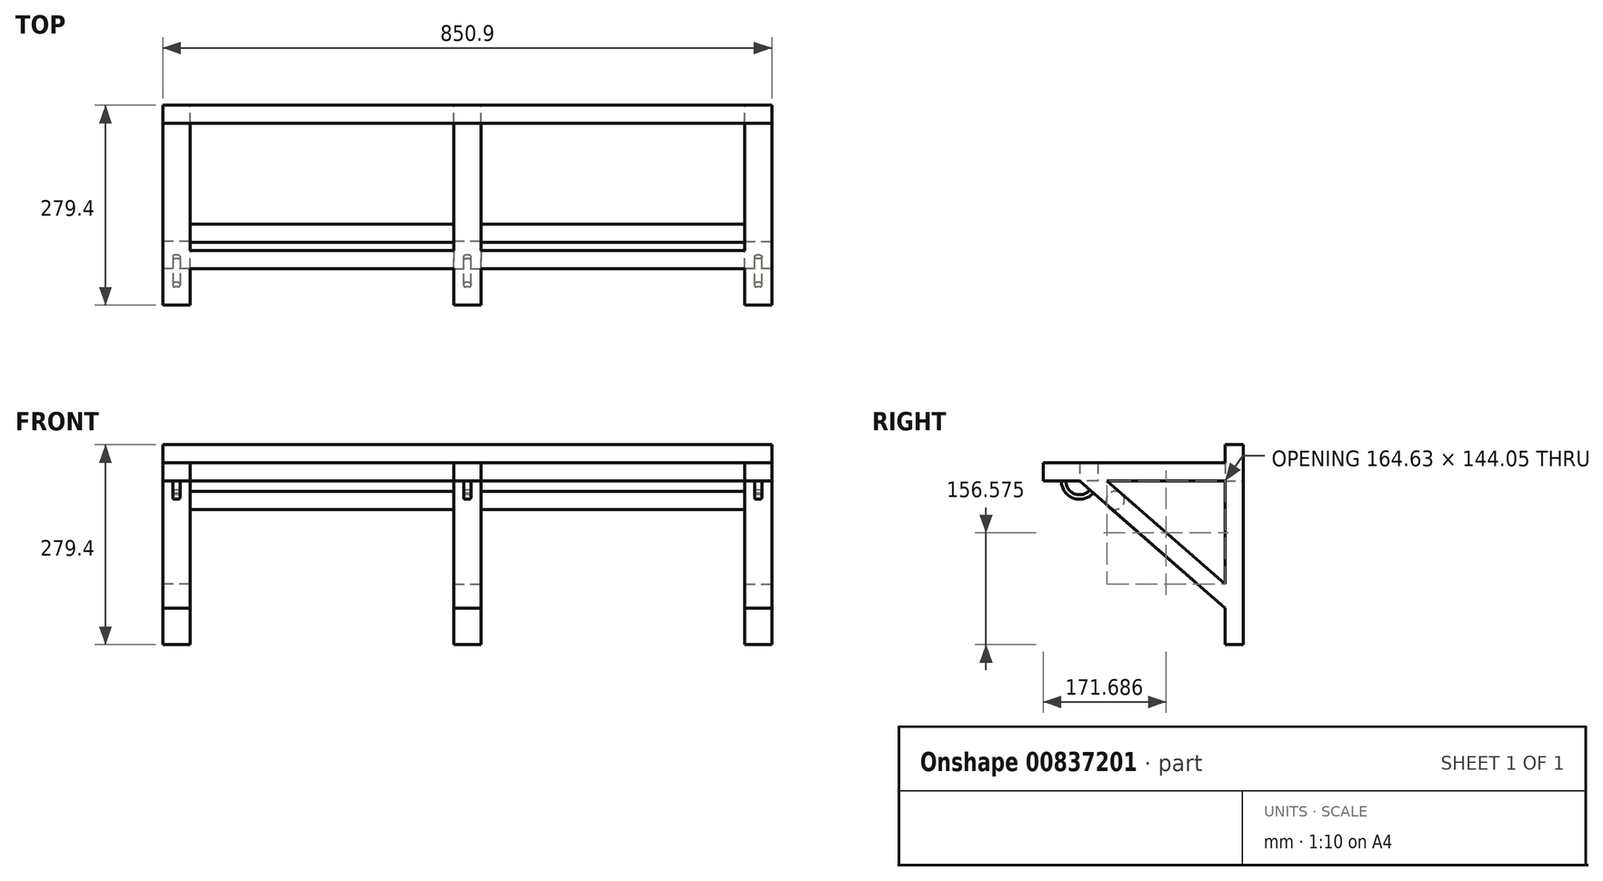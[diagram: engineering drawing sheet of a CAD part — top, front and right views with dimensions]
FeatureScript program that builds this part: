
annotation { "Feature Type Name" : "Feature", "Feature Type Description" : "" }
export const myFeature = defineFeature(function(context is Context, id is Id, definition is map)
    precondition{}
    {
        {
            var Q0;
            Q0=qCreatedBy(makeId("Front.planeOp"),FACE);
            var sketch = newSketch(context, id + "F0", { "sketchPlane" : qUnion([Q0])});
            skLineSegment(sketch, "E0.bottom", {"start": v(19.05, -139.7) * mm, "end": v(-19.05, -139.7) * mm});
            skLineSegment(sketch, "E0.top", {"start": v(19.05, 139.7) * mm, "end": v(-19.05, 139.7) * mm});
            skLineSegment(sketch, "E0.left", {"start": v(19.05, -139.7) * mm, "end": v(19.05, 139.7) * mm});
            skLineSegment(sketch, "E0.right", {"start": v(-19.05, -139.7) * mm, "end": v(-19.05, 139.7) * mm});
            skPoint(sketch, "E0.middle", {"position": v(0, 0) * mm});
            skLineSegment(sketch, "E1.bottom", {"start": v(-387.35, -139.7) * mm, "end": v(-425.45, -139.7) * mm});
            skLineSegment(sketch, "E1.top", {"start": v(-387.35, 139.7) * mm, "end": v(-425.45, 139.7) * mm});
            skLineSegment(sketch, "E1.left", {"start": v(-387.35, -139.7) * mm, "end": v(-387.35, 139.7) * mm});
            skLineSegment(sketch, "E1.right", {"start": v(-425.45, -139.7) * mm, "end": v(-425.45, 139.7) * mm});
            skPoint(sketch, "E1.middle", {"position": v(-406.4, 0) * mm});
            skLineSegment(sketch, "E2.bottom", {"start": v(425.45, -139.7) * mm, "end": v(387.35, -139.7) * mm});
            skLineSegment(sketch, "E2.top", {"start": v(425.45, 139.7) * mm, "end": v(387.35, 139.7) * mm});
            skLineSegment(sketch, "E2.left", {"start": v(425.45, -139.7) * mm, "end": v(425.45, 139.7) * mm});
            skLineSegment(sketch, "E2.right", {"start": v(387.35, -139.7) * mm, "end": v(387.35, 139.7) * mm});
            skPoint(sketch, "E2.middle", {"position": v(406.4, 0) * mm});
            skLineSegment(sketch, "E3.bottom", {"start": v(425.45, 88.9) * mm, "end": v(-425.45, 88.9) * mm});
            skLineSegment(sketch, "E3.top", {"start": v(425.45, 114.3) * mm, "end": v(-425.45, 114.3) * mm});
            skLineSegment(sketch, "E3.left", {"start": v(425.45, 88.9) * mm, "end": v(425.45, 114.3) * mm});
            skLineSegment(sketch, "E3.right", {"start": v(-425.45, 88.9) * mm, "end": v(-425.45, 114.3) * mm});
            skPoint(sketch, "E3.middle", {"position": v(0, 101.6) * mm});
            skSolve(sketch);
        }
        {
            var Q0;
            Q0 = qSketchRegion(id + "F0", true);
            extrude(context, id + "F1", {"entities" : qUnion([Q0]), "depth" : 25.4 * mm, "offsetDistance" : 25.4 * mm});
        }
        {
            var Q0;
            Q0=makeQuery(id+"F1.opExtrude","CAP_FACE",FACE,{"disambiguationData":[OSD([sQuery(id+"F0.wireOp",EDGE,"E0.bottom"),sQuery(id+"F0.wireOp",EDGE,"E0.top"),sQuery(id+"F0.wireOp",EDGE,"E0.left"),sQuery(id+"F0.wireOp",EDGE,"E0.right"),sQuery(id+"F0.wireOp",EDGE,"E1.bottom"),sQuery(id+"F0.wireOp",EDGE,"E1.top"),sQuery(id+"F0.wireOp",EDGE,"E1.left"),sQuery(id+"F0.wireOp",EDGE,"E1.right"),sQuery(id+"F0.wireOp",EDGE,"E2.bottom"),sQuery(id+"F0.wireOp",EDGE,"E2.top"),sQuery(id+"F0.wireOp",EDGE,"E2.left"),sQuery(id+"F0.wireOp",EDGE,"E2.right"),sQuery(id+"F0.wireOp",EDGE,"E3.bottom"),sQuery(id+"F0.wireOp",EDGE,"E3.top"),sQuery(id+"F0.wireOp",EDGE,"E3.left"),sQuery(id+"F0.wireOp",EDGE,"E3.right")])],"isStart":false});
            var sketch = newSketch(context, id + "F2", { "sketchPlane" : qUnion([Q0])});
            skLineSegment(sketch, "E4.bottom", {"start": v(-387.35, 88.9) * mm, "end": v(-425.45, 88.9) * mm});
            skLineSegment(sketch, "E4.top", {"start": v(-387.35, 114.3) * mm, "end": v(-425.45, 114.3) * mm});
            skLineSegment(sketch, "E4.left", {"start": v(-387.35, 88.9) * mm, "end": v(-387.35, 114.3) * mm});
            skLineSegment(sketch, "E4.right", {"start": v(-425.45, 88.9) * mm, "end": v(-425.45, 114.3) * mm});
            skLineSegment(sketch, "E5.bottom", {"start": v(-19.05, 114.3) * mm, "end": v(19.05, 114.3) * mm});
            skLineSegment(sketch, "E5.top", {"start": v(-19.05, 88.9) * mm, "end": v(19.05, 88.9) * mm});
            skLineSegment(sketch, "E5.left", {"start": v(-19.05, 114.3) * mm, "end": v(-19.05, 88.9) * mm});
            skLineSegment(sketch, "E5.right", {"start": v(19.05, 114.3) * mm, "end": v(19.05, 88.9) * mm});
            skLineSegment(sketch, "E6.bottom", {"start": v(387.35, 114.3) * mm, "end": v(425.45, 114.3) * mm});
            skLineSegment(sketch, "E6.top", {"start": v(387.35, 88.9) * mm, "end": v(425.45, 88.9) * mm});
            skLineSegment(sketch, "E6.left", {"start": v(387.35, 114.3) * mm, "end": v(387.35, 88.9) * mm});
            skLineSegment(sketch, "E6.right", {"start": v(425.45, 114.3) * mm, "end": v(425.45, 88.9) * mm});
            skSolve(sketch);
        }
        {
            var Q0;
            Q0 = qSketchRegion(id + "F2", true);
            extrude(context, id + "F3", {"entities" : qUnion([Q0]), "operationType" : NewBodyOperationType.ADD, "depth" : 203.2 * mm, "offsetDistance" : 25.4 * mm});
        }
        {
            var Q0;
            Q0=makeQuery(id+"F3.opExtrude","SWEPT_FACE",FACE,{"disambiguationData":[OSD([sQuery(id+"F2.wireOp",EDGE,"E4.top")])]});
            var sketch = newSketch(context, id + "F4", { "sketchPlane" : qUnion([Q0])});
            skLineSegment(sketch, "E7.bottom", {"start": v(-425.45, -228.6) * mm, "end": v(425.45, -228.6) * mm});
            skLineSegment(sketch, "E7.top", {"start": v(-425.45, -203.2) * mm, "end": v(425.45, -203.2) * mm});
            skLineSegment(sketch, "E7.left", {"start": v(-425.45, -228.6) * mm, "end": v(-425.45, -203.2) * mm});
            skLineSegment(sketch, "E7.right", {"start": v(425.45, -228.6) * mm, "end": v(425.45, -203.2) * mm});
            skSolve(sketch);
        }
        {
            var Q0;
            Q0 = qSketchRegion(id + "F4", true);
            extrude(context, id + "F5", {"entities" : qUnion([Q0]), "operationType" : NewBodyOperationType.ADD, "oppositeDirection" : true, "depth" : 25.4 * mm, "offsetDistance" : 25.4 * mm});
        }
        {
            var Q0;
            Q0=makeQuery(id+"F3.boolean.opBoolean","MERGE",FACE,{"derivedFrom":[makeQuery(id+"F1.opExtrude","SWEPT_FACE",FACE,{"disambiguationData":[OSD([sQuery(id+"F0.wireOp",EDGE,"E1.right"),sQuery(id+"F0.wireOp",EDGE,"E3.right")])]}),makeQuery(id+"F3.opExtrude","SWEPT_FACE",FACE,{"disambiguationData":[OSD([sQuery(id+"F2.wireOp",EDGE,"E4.right")])]})]});
            var sketch = newSketch(context, id + "F6", { "sketchPlane" : qUnion([Q0])});
            skLineSegment(sketch, "E8", {"start": v(228.6, 88.9) * mm, "end": v(25.4, -88.9) * mm});
            skLineSegment(sketch, "E9", {"start": v(25.4, -88.9) * mm, "end": v(25.4, -55.15) * mm});
            skLineSegment(sketch, "E10", {"start": v(25.4, -55.15) * mm, "end": v(190.03, 88.9) * mm});
            skLineSegment(sketch, "E11", {"start": v(190.03, 88.9) * mm, "end": v(228.6, 88.9) * mm});
            skSolve(sketch);
        }
        {
            var Q0;
            Q0 = qSketchRegion(id + "F6", true);
            extrude(context, id + "F7", {"entities" : qUnion([Q0]), "operationType" : NewBodyOperationType.ADD, "oppositeDirection" : true, "depth" : 38.1 * mm, "offsetDistance" : 25.4 * mm});
        }
        {
            var Q0;
            Q0=makeQuery(id+"F3.boolean.opBoolean","MERGE",FACE,{"derivedFrom":[makeQuery(id+"F1.opExtrude","SWEPT_FACE",FACE,{"disambiguationData":[OSD([sQuery(id+"F0.wireOp",EDGE,"E2.left"),sQuery(id+"F0.wireOp",EDGE,"E3.left")])]}),makeQuery(id+"F3.opExtrude","SWEPT_FACE",FACE,{"disambiguationData":[OSD([sQuery(id+"F2.wireOp",EDGE,"E6.right")])]})]});
            var sketch = newSketch(context, id + "F8", { "sketchPlane" : qUnion([Q0])});
            skLineSegment(sketch, "E12", {"start": v(-190.03, 88.9) * mm, "end": v(-25.4, -55.15) * mm});
            skLineSegment(sketch, "E13", {"start": v(-228.6, 88.9) * mm, "end": v(-25.4, -88.9) * mm});
            skLineSegment(sketch, "E14", {"start": v(-190.03, 88.9) * mm, "end": v(-228.6, 88.9) * mm});
            skLineSegment(sketch, "E15", {"start": v(-25.4, -88.9) * mm, "end": v(-25.4, -55.15) * mm});
            skSolve(sketch);
        }
        {
            var Q0;
            Q0 = qSketchRegion(id + "F8", true);
            extrude(context, id + "F9", {"entities" : qUnion([Q0]), "operationType" : NewBodyOperationType.ADD, "oppositeDirection" : true, "depth" : 38.1 * mm, "offsetDistance" : 25.4 * mm});
        }
        {
            var Q0;
            Q0 = qSketchRegion(id + "F6", true);
            extrude(context, id + "F10", {"entities" : qUnion([Q0]), "operationType" : NewBodyOperationType.ADD, "oppositeDirection" : true, "depth" : 38.1 * mm, "offsetDistance" : 25.4 * mm});
        }
        {
            var Q0;
            Q0=makeQuery(id+"F5.boolean.opBoolean","MERGE",FACE,{"derivedFrom":[makeQuery(id+"F3.opExtrude","SWEPT_FACE",FACE,{"disambiguationData":[OSD([sQuery(id+"F2.wireOp",EDGE,"E4.top")])]}),makeQuery(id+"F3.opExtrude","SWEPT_FACE",FACE,{"disambiguationData":[OSD([sQuery(id+"F2.wireOp",EDGE,"E5.bottom")])]}),makeQuery(id+"F3.opExtrude","SWEPT_FACE",FACE,{"disambiguationData":[OSD([sQuery(id+"F2.wireOp",EDGE,"E6.bottom")])]}),makeQuery(id+"F5.opExtrude","CAP_FACE",FACE,{"disambiguationData":[OSD([sQuery(id+"F4.wireOp",EDGE,"E7.bottom"),sQuery(id+"F4.wireOp",EDGE,"E7.top"),sQuery(id+"F4.wireOp",EDGE,"E7.left"),sQuery(id+"F4.wireOp",EDGE,"E7.right")])],"isStart":true})]});
            var sketch = newSketch(context, id + "F11", { "sketchPlane" : qUnion([Q0])});
            skLineSegment(sketch, "E16.top", {"start": v(-425.45, -279.4) * mm, "end": v(-387.35, -279.4) * mm});
            skLineSegment(sketch, "E16.left", {"start": v(-425.45, -228.6) * mm, "end": v(-425.45, -279.4) * mm});
            skLineSegment(sketch, "E16.right", {"start": v(-387.35, -228.6) * mm, "end": v(-387.35, -279.4) * mm});
            skLineSegment(sketch, "E17.top", {"start": v(-19.05, -279.4) * mm, "end": v(19.05, -279.4) * mm});
            skLineSegment(sketch, "E17.left", {"start": v(-19.05, -228.6) * mm, "end": v(-19.05, -279.4) * mm});
            skLineSegment(sketch, "E17.right", {"start": v(19.05, -228.6) * mm, "end": v(19.05, -279.4) * mm});
            skLineSegment(sketch, "E18.top", {"start": v(387.35, -279.4) * mm, "end": v(425.45, -279.4) * mm});
            skLineSegment(sketch, "E18.left", {"start": v(387.35, -228.6) * mm, "end": v(387.35, -279.4) * mm});
            skLineSegment(sketch, "E18.right", {"start": v(425.45, -228.6) * mm, "end": v(425.45, -279.4) * mm});
            skLineSegment(sketch, "E19.top", {"start": v(-425.45, -215.9) * mm, "end": v(-387.35, -215.9) * mm});
            skLineSegment(sketch, "E19.left", {"start": v(-425.45, -228.6) * mm, "end": v(-425.45, -215.9) * mm});
            skLineSegment(sketch, "E19.right", {"start": v(-387.35, -228.6) * mm, "end": v(-387.35, -215.9) * mm});
            skLineSegment(sketch, "E20.top", {"start": v(-19.05, -215.9) * mm, "end": v(19.05, -215.9) * mm});
            skLineSegment(sketch, "E20.left", {"start": v(-19.05, -228.6) * mm, "end": v(-19.05, -215.9) * mm});
            skLineSegment(sketch, "E20.right", {"start": v(19.05, -228.6) * mm, "end": v(19.05, -215.9) * mm});
            skLineSegment(sketch, "E21.bottom", {"start": v(387.35, -215.9) * mm, "end": v(425.45, -215.9) * mm});
            skLineSegment(sketch, "E21.left", {"start": v(387.35, -215.9) * mm, "end": v(387.35, -228.6) * mm});
            skLineSegment(sketch, "E21.right", {"start": v(425.45, -215.9) * mm, "end": v(425.45, -228.6) * mm});
            skSolve(sketch);
        }
        {
            var Q0;
            Q0 = qSketchRegion(id + "F11", true);
            extrude(context, id + "F12", {"entities" : qUnion([Q0]), "operationType" : NewBodyOperationType.ADD, "oppositeDirection" : true, "depth" : 25.4 * mm, "offsetDistance" : 25.4 * mm});
        }
        {
            var Q0;
            Q0=makeQuery(id+"F12.boolean.opBoolean","MERGE",FACE,{"derivedFrom":[makeQuery(id+"F7.boolean.opBoolean","MERGE",FACE,{"derivedFrom":[makeQuery(id+"F3.boolean.opBoolean","MERGE",FACE,{"derivedFrom":[makeQuery(id+"F1.opExtrude","SWEPT_FACE",FACE,{"disambiguationData":[OSD([sQuery(id+"F0.wireOp",EDGE,"E1.right"),sQuery(id+"F0.wireOp",EDGE,"E3.right")])]}),makeQuery(id+"F3.opExtrude","SWEPT_FACE",FACE,{"disambiguationData":[OSD([sQuery(id+"F2.wireOp",EDGE,"E4.right")])]})]}),makeQuery(id+"F7.opExtrude","CAP_FACE",FACE,{"disambiguationData":[OSD([sQuery(id+"F6.wireOp",EDGE,"E8"),sQuery(id+"F6.wireOp",EDGE,"E9"),sQuery(id+"F6.wireOp",EDGE,"E10"),sQuery(id+"F6.wireOp",EDGE,"E11")])],"isStart":true})]}),makeQuery(id+"F12.opExtrude","SWEPT_FACE",FACE,{"disambiguationData":[OSD([sQuery(id+"F11.wireOp",EDGE,"E16.left"),sQuery(id+"F11.wireOp",EDGE,"E19.left")])]})]});
            cPlane(context, id + "F13", {"entities" : qUnion([Q0]), "cplaneType" : CPlaneType.OFFSET, "offset" : 19.05 * mm, "oppositeDirection" : true, "width" : 152.4 * mm, "height" : 152.4 * mm});
        }
        {
            var Q0;
            Q0=qCreatedBy(id+"F13.planeOp",FACE);
            var sketch = newSketch(context, id + "F14", { "sketchPlane" : qUnion([Q0])});
            skCircle(sketch, "E22", {"center": v(228.6, 88.9) * mm, "radius": 25.4 * mm});
            skCircle(sketch, "E23", {"center": v(228.6, 88.9) * mm, "radius": 19.05 * mm});
            skSolve(sketch);
        }
        {
            var Q0;
            Q0 = qSketchRegion(id + "F14", true);
            extrude(context, id + "F15", {"entities" : qUnion([Q0]), "operationType" : NewBodyOperationType.ADD, "oppositeDirection" : true, "depth" : 5.08 * mm, "offsetDistance" : 25.4 * mm, "hasSecondDirection" : true, "secondDirectionOppositeDirection" : false, "secondDirectionDepth" : 5.08 * mm});
        }
        {
            var Q0;
            Q0=makeQuery(id+"F12.boolean.opBoolean","MERGE",FACE,{"derivedFrom":[makeQuery(id+"F9.boolean.opBoolean","MERGE",FACE,{"derivedFrom":[makeQuery(id+"F3.boolean.opBoolean","MERGE",FACE,{"derivedFrom":[makeQuery(id+"F1.opExtrude","SWEPT_FACE",FACE,{"disambiguationData":[OSD([sQuery(id+"F0.wireOp",EDGE,"E2.left"),sQuery(id+"F0.wireOp",EDGE,"E3.left")])]}),makeQuery(id+"F3.opExtrude","SWEPT_FACE",FACE,{"disambiguationData":[OSD([sQuery(id+"F2.wireOp",EDGE,"E6.right")])]})]}),makeQuery(id+"F9.opExtrude","CAP_FACE",FACE,{"disambiguationData":[OSD([sQuery(id+"F8.wireOp",EDGE,"E12"),sQuery(id+"F8.wireOp",EDGE,"E13"),sQuery(id+"F8.wireOp",EDGE,"E14"),sQuery(id+"F8.wireOp",EDGE,"E15")])],"isStart":true})]}),makeQuery(id+"F12.opExtrude","SWEPT_FACE",FACE,{"disambiguationData":[OSD([sQuery(id+"F11.wireOp",EDGE,"E18.right"),sQuery(id+"F11.wireOp",EDGE,"E21.right")])]})]});
            cPlane(context, id + "F16", {"entities" : qUnion([Q0]), "cplaneType" : CPlaneType.OFFSET, "offset" : 19.05 * mm, "oppositeDirection" : true, "width" : 152.4 * mm, "height" : 152.4 * mm});
        }
        {
            var Q0;
            Q0=qCreatedBy(id+"F16.planeOp",FACE);
            var sketch = newSketch(context, id + "F17", { "sketchPlane" : qUnion([Q0])});
            skCircle(sketch, "E24", {"center": v(-228.6, 88.9) * mm, "radius": 25.4 * mm});
            skCircle(sketch, "E25", {"center": v(-228.6, 88.9) * mm, "radius": 19.05 * mm});
            skSolve(sketch);
        }
        {
            var Q0;
            Q0 = qSketchRegion(id + "F17", true);
            extrude(context, id + "F18", {"entities" : qUnion([Q0]), "operationType" : NewBodyOperationType.ADD, "depth" : 5.08 * mm, "offsetDistance" : 25.4 * mm, "hasSecondDirection" : true, "secondDirectionOppositeDirection" : true, "secondDirectionDepth" : 5.08 * mm});
        }
        {
            var Q0;
            Q0=makeQuery(id+"F18.opExtrude","CAP_EDGE",EDGE,{"disambiguationData":[OSD([sQuery(id+"F17.wireOp",EDGE,"E24")])],"isStart":false});
            var Q1;
            Q1=makeQuery(id+"F18.opExtrude","CAP_EDGE",EDGE,{"disambiguationData":[OSD([sQuery(id+"F17.wireOp",EDGE,"E25")])],"isStart":false});
            var Q2;
            Q2=makeQuery(id+"F18.opExtrude","CAP_EDGE",EDGE,{"disambiguationData":[OSD([sQuery(id+"F17.wireOp",EDGE,"E25")])],"isStart":true});
            var Q3;
            Q3=makeQuery(id+"F18.opExtrude","CAP_EDGE",EDGE,{"disambiguationData":[OSD([sQuery(id+"F17.wireOp",EDGE,"E24")])],"isStart":true});
            var Q4;
            Q4=makeQuery(id+"F15.opExtrude","CAP_EDGE",EDGE,{"disambiguationData":[OSD([sQuery(id+"F14.wireOp",EDGE,"E23")])],"isStart":false});
            var Q5;
            Q5=makeQuery(id+"F15.opExtrude","CAP_EDGE",EDGE,{"disambiguationData":[OSD([sQuery(id+"F14.wireOp",EDGE,"E22")])],"isStart":false});
            var Q6;
            Q6=makeQuery(id+"F15.opExtrude","CAP_EDGE",EDGE,{"disambiguationData":[OSD([sQuery(id+"F14.wireOp",EDGE,"E23")])],"isStart":true});
            var Q7;
            Q7=makeQuery(id+"F15.opExtrude","CAP_EDGE",EDGE,{"disambiguationData":[OSD([sQuery(id+"F14.wireOp",EDGE,"E22")])],"isStart":true});
            fillet(context, id + "F19", {"entities" : qUnion([Q0, Q1, Q2, Q3, Q4, Q5, Q6, Q7]), "radius" : 2.54 * mm, "tangentPropagation" : true, "allowEdgeOverflow" : false});
        }
        {
            var Q0;
            {var subQ0=sQuery(id+"F0.wireOp",EDGE,"E1.left");var subQ1=sQuery(id+"F0.wireOp",EDGE,"E1.top");var subQ2=sQuery(id+"F0.wireOp",EDGE,"E3.top");var subQ4=sQuery(id+"F0.wireOp",EDGE,"E3.right");var subQ5=sQuery(id+"F0.wireOp",EDGE,"E1.right");var subQ6=sQuery(id+"F0.wireOp",EDGE,"E0.right");var subQ7=makeQuery(id+"F1.opExtrude","CAP_FACE",FACE,{"disambiguationData":[OSD([sQuery(id+"F0.wireOp",EDGE,"E0.bottom"),sQuery(id+"F0.wireOp",EDGE,"E0.top"),sQuery(id+"F0.wireOp",EDGE,"E0.left"),subQ6,sQuery(id+"F0.wireOp",EDGE,"E1.bottom"),subQ1,subQ0,subQ5,sQuery(id+"F0.wireOp",EDGE,"E2.bottom"),sQuery(id+"F0.wireOp",EDGE,"E2.top"),sQuery(id+"F0.wireOp",EDGE,"E2.left"),sQuery(id+"F0.wireOp",EDGE,"E2.right"),sQuery(id+"F0.wireOp",EDGE,"E3.bottom"),subQ2,sQuery(id+"F0.wireOp",EDGE,"E3.left"),subQ4])],"isStart":false});Q0=makeQuery(id+"F3.boolean.opBoolean","SPLIT",FACE,{"disambiguationData":[TD([subQ7,makeQuery(id+"F1.opExtrude","SWEPT_FACE",FACE,{"disambiguationData":[OSD([subQ1])]}),makeQuery(id+"F1.opExtrude","SWEPT_FACE",FACE,{"disambiguationData":[OSD([subQ0]),TDD([makeQuery(id+"F0.imprint","IMPRINT",EDGE,{"disambiguationData":[TD([[makeQuery(id+"F0.imprint","INTERSECT",VERTEX,{"derivedFrom":[subQ1,subQ0]}),1.0]])],"derivedFrom":subQ0})])]}),makeQuery(id+"F1.opExtrude","SWEPT_FACE",FACE,{"disambiguationData":[OSD([subQ5,subQ4])]}),makeQuery(id+"F1.opExtrude","SWEPT_FACE",FACE,{"disambiguationData":[OSD([subQ2]),TDD([makeQuery(id+"F0.imprint","IMPRINT",EDGE,{"disambiguationData":[TD([[makeQuery(id+"F0.imprint","INTERSECT",VERTEX,{"derivedFrom":[subQ6,subQ2]}),-1.0]])],"derivedFrom":subQ2})])]}),makeQuery(id+"F3.opExtrude","SWEPT_FACE",FACE,{"disambiguationData":[OSD([sQuery(id+"F2.wireOp",EDGE,"E4.top")])]}),makeQuery(id+"F3.opExtrude","SWEPT_FACE",FACE,{"disambiguationData":[OSD([sQuery(id+"F2.wireOp",EDGE,"E4.left")])]}),makeQuery(id+"F3.opExtrude","SWEPT_FACE",FACE,{"disambiguationData":[OSD([sQuery(id+"F2.wireOp",EDGE,"E4.right")])]})])],"derivedFrom":subQ7});}
            var sketch = newSketch(context, id + "F20", { "sketchPlane" : qUnion([Q0])});
            skLineSegment(sketch, "E26.bottom", {"start": v(-387.35, 139.7) * mm, "end": v(387.44, 139.7) * mm});
            skLineSegment(sketch, "E26.top", {"start": v(-387.35, 114.3) * mm, "end": v(387.44, 114.3) * mm});
            skLineSegment(sketch, "E26.left", {"start": v(-387.35, 139.7) * mm, "end": v(-387.35, 114.3) * mm});
            skLineSegment(sketch, "E26.right", {"start": v(387.44, 139.7) * mm, "end": v(387.44, 114.3) * mm});
            skSolve(sketch);
        }
        {
            var Q0;
            Q0 = qSketchRegion(id + "F20", true);
            extrude(context, id + "F21", {"entities" : qUnion([Q0]), "operationType" : NewBodyOperationType.ADD, "oppositeDirection" : true, "depth" : 25.4 * mm, "offsetDistance" : 25.4 * mm});
        }
        {
            var Q0;
            Q0=qCreatedBy(makeId("Right.planeOp"),FACE);
            var sketch = newSketch(context, id + "F22", { "sketchPlane" : qUnion([Q0])});
            skLineSegment(sketch, "E27", {"start": v(-20.84, -59.14) * mm, "end": v(-208.75, 105.29) * mm});
            skLineSegment(sketch, "E28", {"start": v(-208.75, 105.29) * mm, "end": v(-247.33, 105.29) * mm});
            skLineSegment(sketch, "E29", {"start": v(-247.33, 105.29) * mm, "end": v(-20.84, -92.9) * mm});
            skLineSegment(sketch, "E30", {"start": v(-20.84, -92.9) * mm, "end": v(-20.84, -59.14) * mm});
            skSolve(sketch);
        }
        {
            var Q0;
            Q0 = qSketchRegion(id + "F22", true);
            extrude(context, id + "F23", {"entities" : qUnion([Q0]), "operationType" : NewBodyOperationType.ADD, "depth" : 19.05 * mm, "offsetDistance" : 25.4 * mm, "hasSecondDirection" : true, "secondDirectionOppositeDirection" : true, "secondDirectionDepth" : 19.05 * mm});
        }
        {
            var Q0;
            Q0=qCreatedBy(makeId("Right.planeOp"),FACE);
            var sketch = newSketch(context, id + "F24", { "sketchPlane" : qUnion([Q0])});
            skCircle(sketch, "E31", {"center": v(-228.6, 88.9) * mm, "radius": 25.4 * mm});
            skCircle(sketch, "E32", {"center": v(-228.6, 88.9) * mm, "radius": 19.05 * mm});
            skSolve(sketch);
        }
        {
            var Q0;
            Q0 = qSketchRegion(id + "F24", true);
            extrude(context, id + "F25", {"entities" : qUnion([Q0]), "operationType" : NewBodyOperationType.ADD, "depth" : 5.08 * mm, "offsetDistance" : 25.4 * mm, "hasSecondDirection" : true, "secondDirectionOppositeDirection" : true, "secondDirectionDepth" : 5.08 * mm});
        }
        {
            var Q0;
            Q0=makeQuery(id+"F25.opExtrude","CAP_EDGE",EDGE,{"disambiguationData":[OSD([sQuery(id+"F24.wireOp",EDGE,"E32")])],"isStart":false});
            var Q1;
            Q1=makeQuery(id+"F25.opExtrude","CAP_EDGE",EDGE,{"disambiguationData":[OSD([sQuery(id+"F24.wireOp",EDGE,"E31")])],"isStart":false});
            var Q2;
            Q2=makeQuery(id+"F25.opExtrude","CAP_EDGE",EDGE,{"disambiguationData":[OSD([sQuery(id+"F24.wireOp",EDGE,"E32")])],"isStart":true});
            var Q3;
            Q3=makeQuery(id+"F25.opExtrude","CAP_EDGE",EDGE,{"disambiguationData":[OSD([sQuery(id+"F24.wireOp",EDGE,"E31")])],"isStart":true});
            fillet(context, id + "F26", {"entities" : qUnion([Q0, Q1, Q2, Q3]), "radius" : 2.54 * mm, "tangentPropagation" : true, "allowEdgeOverflow" : false});
        }
        {
            var Q0;
            Q0=makeQuery(id+"F12.boolean.opBoolean","MERGE",FACE,{"derivedFrom":[makeQuery(id+"F9.boolean.opBoolean","MERGE",FACE,{"derivedFrom":[makeQuery(id+"F3.boolean.opBoolean","MERGE",FACE,{"derivedFrom":[makeQuery(id+"F1.opExtrude","SWEPT_FACE",FACE,{"disambiguationData":[OSD([sQuery(id+"F0.wireOp",EDGE,"E2.left"),sQuery(id+"F0.wireOp",EDGE,"E3.left")])]}),makeQuery(id+"F3.opExtrude","SWEPT_FACE",FACE,{"disambiguationData":[OSD([sQuery(id+"F2.wireOp",EDGE,"E6.right")])]})]}),makeQuery(id+"F9.opExtrude","CAP_FACE",FACE,{"disambiguationData":[OSD([sQuery(id+"F8.wireOp",EDGE,"E12"),sQuery(id+"F8.wireOp",EDGE,"E13"),sQuery(id+"F8.wireOp",EDGE,"E14"),sQuery(id+"F8.wireOp",EDGE,"E15")])],"isStart":true})]}),makeQuery(id+"F12.opExtrude","SWEPT_FACE",FACE,{"disambiguationData":[OSD([sQuery(id+"F11.wireOp",EDGE,"E18.right"),sQuery(id+"F11.wireOp",EDGE,"E21.right")])]})]});
            var sketch = newSketch(context, id + "F27", { "sketchPlane" : qUnion([Q0])});
            skCircle(sketch, "E33", {"center": v(-178.66, 62.08) * mm, "radius": 12.7 * mm});
            skSolve(sketch);
        }
        {
            var Q0;
            Q0 = qSketchRegion(id + "F27", true);
            extrude(context, id + "F28", {"entities" : qUnion([Q0]), "operationType" : NewBodyOperationType.ADD, "oppositeDirection" : true, "depth" : 850.9 * mm, "offsetDistance" : 25.4 * mm});
        }
    });
